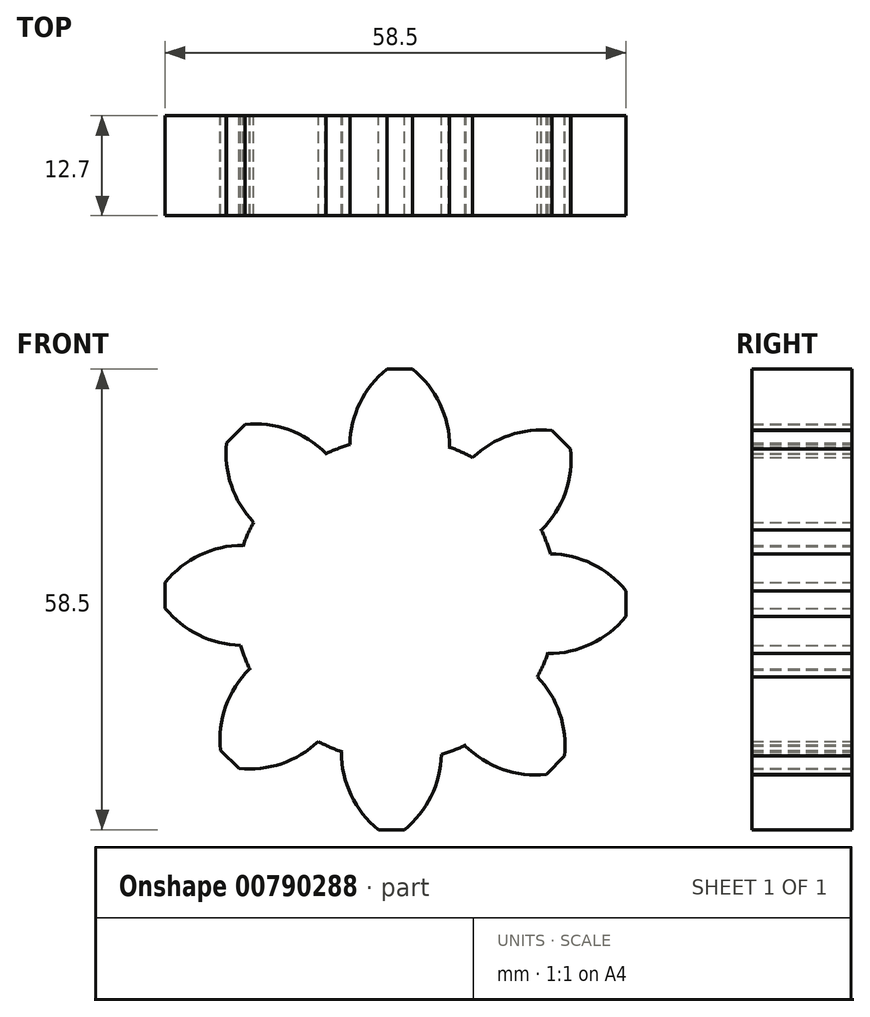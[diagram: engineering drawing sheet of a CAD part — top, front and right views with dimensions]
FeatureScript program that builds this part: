
annotation { "Feature Type Name" : "Feature", "Feature Type Description" : "" }
export const myFeature = defineFeature(function(context is Context, id is Id, definition is map)
    precondition{}
    {
        {
            var Q0;
            Q0=qCreatedBy(makeId("Front.planeOp"),FACE);
            var sketch = newSketch(context, id + "F0", { "sketchPlane" : qUnion([Q0])});
            skArc(sketch, "E0", {"start": v(6.88, 19.38) * mm, "mid": v(5.65, 24.85) * mm, "end": v(2.18, 29.25) * mm});
            skArc(sketch, "E1", {"start": v(-1.1, 29.25) * mm, "mid": v(-4.58, 24.85) * mm, "end": v(-5.82, 19.38) * mm});
            skLineSegment(sketch, "E2", {"start": v(-5.82, 19.38) * mm, "end": v(6.88, 19.38) * mm});
            skLineSegment(sketch, "E3", {"start": v(-1.1, 29.25) * mm, "end": v(2.18, 29.25) * mm});
            skSolve(sketch);
        }
        {
            var Q0;
            Q0=qCreatedBy(makeId("Front.planeOp"),FACE);
            var sketch = newSketch(context, id + "F1", { "sketchPlane" : qUnion([Q0])});
            skCircle(sketch, "E4", {"center": v(0, 0) * mm, "radius": 20.52 * mm});
            skSolve(sketch);
        }
        {
            var Q0;
            Q0=makeQuery(id+"F0.imprint","IMPRINT",FACE,{"disambiguationData":[TD([[makeQuery(id+"F0.imprint","IMPRINT",EDGE,{"derivedFrom":sQuery(id+"F0.wireOp",EDGE,"E0")}),1.0]])]});
            extrude(context, id + "F2", {"entities" : qUnion([Q0]), "depth" : 12.7 * mm, "offsetDistance" : 25.4 * mm});
        }
        {
            var Q0;
            Q0=makeQuery(id+"F1.imprint","IMPRINT",FACE,{"disambiguationData":[TD([[makeQuery(id+"F1.imprint","IMPRINT",EDGE,{"derivedFrom":sQuery(id+"F1.wireOp",EDGE,"E4")}),1.0]])]});
            extrude(context, id + "F3", {"entities" : qUnion([Q0]), "depth" : 12.7 * mm, "offsetDistance" : 25.4 * mm});
        }
        {
            var Q0;
            Q0=makeQuery(id+"F2.opExtrude","SWEPT_BODY",BODY,{"disambiguationData":[OSD([sQuery(id+"F0.wireOp",EDGE,"E0"),sQuery(id+"F0.wireOp",EDGE,"E1"),sQuery(id+"F0.wireOp",EDGE,"E2"),sQuery(id+"F0.wireOp",EDGE,"E3")])]});
            var Q1;
            Q1=makeQuery(id+"F3.opExtrude","SWEPT_FACE",FACE,{"disambiguationData":[OSD([sQuery(id+"F1.wireOp",EDGE,"E4")])]});
            circularPattern(context, id + "F4", {"operationType" : NewBodyOperationType.ADD, "entities" : qUnion([Q0]), "axis" : qUnion([Q1]), "angle" : 360 * degree, "instanceCount" : 8, "equalSpace" : true});
        }
        {
            var Q0;
            Q0=qCreatedBy(makeId("Front.planeOp"),FACE);
            var sketch = newSketch(context, id + "F5", { "sketchPlane" : qUnion([Q0])});
            skArc(sketch, "E5", {"start": v(-83.95, 40.77) * mm, "mid": v(-85.2, 46.24) * mm, "end": v(-88.66, 50.64) * mm});
            skArc(sketch, "E6", {"start": v(-91.95, 50.64) * mm, "mid": v(-95.42, 46.24) * mm, "end": v(-96.65, 40.77) * mm});
            skLineSegment(sketch, "E7", {"start": v(-96.65, 40.77) * mm, "end": v(-83.95, 40.77) * mm});
            skLineSegment(sketch, "E8", {"start": v(-91.95, 50.64) * mm, "end": v(-88.66, 50.64) * mm});
            skSolve(sketch);
        }
        {
            var Q0;
            Q0=qCreatedBy(makeId("Front.planeOp"),FACE);
            var sketch = newSketch(context, id + "F6", { "sketchPlane" : qUnion([Q0])});
            skCircle(sketch, "E9", {"center": v(-88.56, 0) * mm, "radius": 43.07 * mm});
            skSolve(sketch);
        }
        {
            var Q0;
            Q0=makeQuery(id+"F5.imprint","IMPRINT",FACE,{"disambiguationData":[TD([[makeQuery(id+"F5.imprint","IMPRINT",EDGE,{"derivedFrom":sQuery(id+"F5.wireOp",EDGE,"E5")}),1.0]])]});
            extrude(context, id + "F7", {"entities" : qUnion([Q0]), "depth" : 12.7 * mm, "offsetDistance" : 25.4 * mm});
        }
        {
            var Q0;
            Q0=makeQuery(id+"F6.imprint","IMPRINT",FACE,{"disambiguationData":[TD([[makeQuery(id+"F6.imprint","IMPRINT",EDGE,{"derivedFrom":sQuery(id+"F6.wireOp",EDGE,"E9")}),1.0]])]});
            extrude(context, id + "F8", {"entities" : qUnion([Q0]), "operationType" : NewBodyOperationType.ADD, "depth" : 12.7 * mm, "offsetDistance" : 25.4 * mm});
        }
        {
            var Q0;
            Q0=makeQuery(id+"F7.opExtrude","SWEPT_BODY",BODY,{"disambiguationData":[OSD([sQuery(id+"F5.wireOp",EDGE,"E5"),sQuery(id+"F5.wireOp",EDGE,"E6"),sQuery(id+"F5.wireOp",EDGE,"E7"),sQuery(id+"F5.wireOp",EDGE,"E8")])]});
            var Q1;
            Q1=makeQuery(id+"F8.opExtrude","SWEPT_FACE",FACE,{"disambiguationData":[OSD([sQuery(id+"F6.wireOp",EDGE,"E9")])]});
            circularPattern(context, id + "F9", {"operationType" : NewBodyOperationType.ADD, "entities" : qUnion([Q0]), "axis" : qUnion([Q1]), "angle" : 360 * degree, "instanceCount" : 15, "equalSpace" : true});
        }
        {
            var Q0;
            Q0=makeQuery(id+"F9.opPattern","COPY",BODY,{"derivedFrom":makeQuery(id+"F7.opExtrude","SWEPT_BODY",BODY,{"disambiguationData":[OSD([sQuery(id+"F5.wireOp",EDGE,"E5"),sQuery(id+"F5.wireOp",EDGE,"E6"),sQuery(id+"F5.wireOp",EDGE,"E7"),sQuery(id+"F5.wireOp",EDGE,"E8")])]}),"instanceName":"13"});
            var Q1;
            Q1=makeQuery(id+"F9.opPattern","COPY",BODY,{"derivedFrom":makeQuery(id+"F7.opExtrude","SWEPT_BODY",BODY,{"disambiguationData":[OSD([sQuery(id+"F5.wireOp",EDGE,"E5"),sQuery(id+"F5.wireOp",EDGE,"E6"),sQuery(id+"F5.wireOp",EDGE,"E7"),sQuery(id+"F5.wireOp",EDGE,"E8")])]}),"instanceName":"8"});
            var Q2;
            Q2=makeQuery(id+"F7.opExtrude","SWEPT_BODY",BODY,{"disambiguationData":[OSD([sQuery(id+"F5.wireOp",EDGE,"E5"),sQuery(id+"F5.wireOp",EDGE,"E6"),sQuery(id+"F5.wireOp",EDGE,"E7"),sQuery(id+"F5.wireOp",EDGE,"E8")])]});
            var Q3;
            Q3=makeQuery(id+"F9.opPattern","COPY",BODY,{"derivedFrom":makeQuery(id+"F7.opExtrude","SWEPT_BODY",BODY,{"disambiguationData":[OSD([sQuery(id+"F5.wireOp",EDGE,"E5"),sQuery(id+"F5.wireOp",EDGE,"E6"),sQuery(id+"F5.wireOp",EDGE,"E7"),sQuery(id+"F5.wireOp",EDGE,"E8")])]}),"instanceName":"14"});
            var Q4;
            Q4=makeQuery(id+"F9.opPattern","COPY",BODY,{"derivedFrom":makeQuery(id+"F7.opExtrude","SWEPT_BODY",BODY,{"disambiguationData":[OSD([sQuery(id+"F5.wireOp",EDGE,"E5"),sQuery(id+"F5.wireOp",EDGE,"E6"),sQuery(id+"F5.wireOp",EDGE,"E7"),sQuery(id+"F5.wireOp",EDGE,"E8")])]}),"instanceName":"6"});
            var Q5;
            Q5=makeQuery(id+"F9.opPattern","COPY",BODY,{"derivedFrom":makeQuery(id+"F7.opExtrude","SWEPT_BODY",BODY,{"disambiguationData":[OSD([sQuery(id+"F5.wireOp",EDGE,"E5"),sQuery(id+"F5.wireOp",EDGE,"E6"),sQuery(id+"F5.wireOp",EDGE,"E7"),sQuery(id+"F5.wireOp",EDGE,"E8")])]}),"instanceName":"4"});
            var Q6;
            Q6=makeQuery(id+"F9.opPattern","COPY",BODY,{"derivedFrom":makeQuery(id+"F7.opExtrude","SWEPT_BODY",BODY,{"disambiguationData":[OSD([sQuery(id+"F5.wireOp",EDGE,"E5"),sQuery(id+"F5.wireOp",EDGE,"E6"),sQuery(id+"F5.wireOp",EDGE,"E7"),sQuery(id+"F5.wireOp",EDGE,"E8")])]}),"instanceName":"10"});
            var Q7;
            Q7=makeQuery(id+"F9.opPattern","COPY",BODY,{"derivedFrom":makeQuery(id+"F7.opExtrude","SWEPT_BODY",BODY,{"disambiguationData":[OSD([sQuery(id+"F5.wireOp",EDGE,"E5"),sQuery(id+"F5.wireOp",EDGE,"E6"),sQuery(id+"F5.wireOp",EDGE,"E7"),sQuery(id+"F5.wireOp",EDGE,"E8")])]}),"instanceName":"9"});
            var Q8;
            Q8=makeQuery(id+"F9.opPattern","COPY",BODY,{"derivedFrom":makeQuery(id+"F7.opExtrude","SWEPT_BODY",BODY,{"disambiguationData":[OSD([sQuery(id+"F5.wireOp",EDGE,"E5"),sQuery(id+"F5.wireOp",EDGE,"E6"),sQuery(id+"F5.wireOp",EDGE,"E7"),sQuery(id+"F5.wireOp",EDGE,"E8")])]}),"instanceName":"12"});
            var Q9;
            Q9=makeQuery(id+"F9.opPattern","COPY",BODY,{"derivedFrom":makeQuery(id+"F7.opExtrude","SWEPT_BODY",BODY,{"disambiguationData":[OSD([sQuery(id+"F5.wireOp",EDGE,"E5"),sQuery(id+"F5.wireOp",EDGE,"E6"),sQuery(id+"F5.wireOp",EDGE,"E7"),sQuery(id+"F5.wireOp",EDGE,"E8")])]}),"instanceName":"1"});
            var Q10;
            Q10=makeQuery(id+"F9.opPattern","COPY",BODY,{"derivedFrom":makeQuery(id+"F7.opExtrude","SWEPT_BODY",BODY,{"disambiguationData":[OSD([sQuery(id+"F5.wireOp",EDGE,"E5"),sQuery(id+"F5.wireOp",EDGE,"E6"),sQuery(id+"F5.wireOp",EDGE,"E7"),sQuery(id+"F5.wireOp",EDGE,"E8")])]}),"instanceName":"3"});
            var Q11;
            Q11=makeQuery(id+"F9.opPattern","COPY",BODY,{"derivedFrom":makeQuery(id+"F7.opExtrude","SWEPT_BODY",BODY,{"disambiguationData":[OSD([sQuery(id+"F5.wireOp",EDGE,"E5"),sQuery(id+"F5.wireOp",EDGE,"E6"),sQuery(id+"F5.wireOp",EDGE,"E7"),sQuery(id+"F5.wireOp",EDGE,"E8")])]}),"instanceName":"11"});
            var Q12;
            Q12=makeQuery(id+"F9.opPattern","COPY",BODY,{"derivedFrom":makeQuery(id+"F7.opExtrude","SWEPT_BODY",BODY,{"disambiguationData":[OSD([sQuery(id+"F5.wireOp",EDGE,"E5"),sQuery(id+"F5.wireOp",EDGE,"E6"),sQuery(id+"F5.wireOp",EDGE,"E7"),sQuery(id+"F5.wireOp",EDGE,"E8")])]}),"instanceName":"5"});
            var Q13;
            Q13=makeQuery(id+"F9.opPattern","COPY",BODY,{"derivedFrom":makeQuery(id+"F7.opExtrude","SWEPT_BODY",BODY,{"disambiguationData":[OSD([sQuery(id+"F5.wireOp",EDGE,"E5"),sQuery(id+"F5.wireOp",EDGE,"E6"),sQuery(id+"F5.wireOp",EDGE,"E7"),sQuery(id+"F5.wireOp",EDGE,"E8")])]}),"instanceName":"7"});
            var Q14;
            Q14=makeQuery(id+"F9.opPattern","COPY",BODY,{"derivedFrom":makeQuery(id+"F7.opExtrude","SWEPT_BODY",BODY,{"disambiguationData":[OSD([sQuery(id+"F5.wireOp",EDGE,"E5"),sQuery(id+"F5.wireOp",EDGE,"E6"),sQuery(id+"F5.wireOp",EDGE,"E7"),sQuery(id+"F5.wireOp",EDGE,"E8")])]}),"instanceName":"2"});
            deleteBodies(context, id + "F10", {"entities" : qUnion([Q0, Q1, Q2, Q3, Q4, Q5, Q6, Q7, Q8, Q9, Q10, Q11, Q12, Q13, Q14])});
        }
    });
